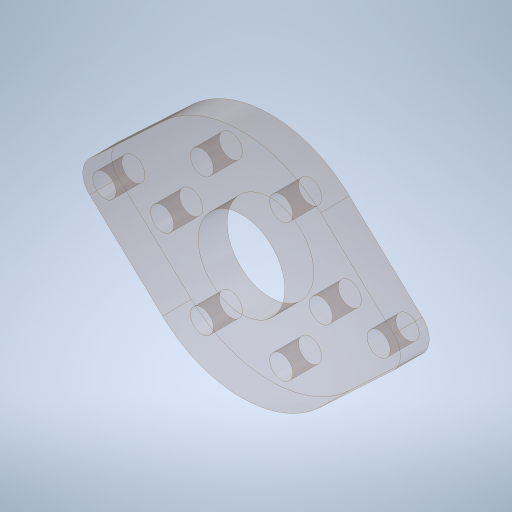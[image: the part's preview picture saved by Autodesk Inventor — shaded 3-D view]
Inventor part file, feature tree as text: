
AUTODESK INVENTOR PART (.ipt)
format: ipt  version: 2023.4 (Build 274418000, 418)  size: 297,984 bytes
history: native  units: in
note: dims shown in document units (in); Inventor stores cm internally (conversion verified against a paired STEP export)
features: sketch x1, extrude x1, hole x1
ambient origin geometry x8: Origin, YZ Plane, XZ Plane, XY Plane, X Axis, Y Axis, Z Axis, Center Point
bodies: Solid1 (feature_tree)
feature tree (3):
  sketch  "Sketch1"  dims[d0=0.75in d1=2.0in d2=0.375in d3=1.375in d4=2.3622in d6=360.0deg d8=0.25in d9=0.0in d10=0.201in d11=0.75in d12=0.385in d13=0.25in d14=0.5635in d15=1.0in d16=0.8108in]
  extrude  "Extrusion1"  Depth=2.0in
  hole  "Hole1"  [1 undecoded]
note: 1 required parameter value undecoded (feature->parameter linkage not recoverable at this tier; creation-order binding heuristic only, values carry confidence <= 0.55)
